# Revit family: PRD_FrankeWS_WCAndWshbsnCmbndUnts_HEAVYDUTYWCWashbasinCombination_HDTX806L_HDTX806M_HDTX806R
name_source: partatom
category: Plumbing Fixtures
revit_build: Autodesk Revit 2018 (Build: 20190510_1515(x64)
units: mm (PartAtom-declared; Revit-internal decimal feet)

## family parameters
Cut with Voids When Loaded = No
Host = Face
OmniClass Number = 23.45.05.14.31
OmniClass Title = Combination Toilets
Part Type = Normal
Room Calculation Point = No
Round Connector Dimension = Use Diameter
Shared = No

## types (3) — shared parameters
AssetType = Fixed
BodyMaterial = PRD_AR_StainlessSteel_SatinFinished
BodyWidth = 390.00 mm
Category = Pr_40_20_93_86, WC and washbasin combined units
DrainSize = 100 mm  [stored 0.328084 ft]
DurationUnit = year
Finish = Satin finish
FloorFixingJogglePlate = No
FrontAccessPanel = No
IfcExportAs = IfcSanitaryTerminalType
IfcExportType = WASHHANDBASIN
InletSize = DN 15
IntakeSize = 15  [stored 0.0492126 ft]
IntegralAccessories = Including fixing material
Manufacturer = KWC Group AG
ManufacturerName = KWC Group AG
ManufacturerURL = www.kwc.com
Material = stainless steel
MaterialCode = 1.4301 Chrome Nickel steel V2A
MaterialThicknessBody = 2.00 mm
MaterialThicknessWC = 1.50 mm
Mounting = BackToWall
NBSDescription = WC and washbasin combined units
NBSReference = 45-35-70/410
NominalHeight = 1000 mm  [stored 3.28084 ft]
OutletSize = DN 100
Overflow = No
PipeworkMaterial = Stainless steel
ProductInformation = https://pim.kwc.com
SelfClosingPushButtons = Electronical
ShroudDesign = Round shape
SoapDish = No
SpoutLength = 83.00 mm
TailorMade = No
TapWithIntegratedBubbler = No
ToiletRollHolderDiameter = 153.00 mm
TypeOfFlushingFitting = WC cistern
TypeOfMounting = Bolt mounting
TypeOfToiletSeat = No seat
TypeOfWC = Floor standing
URL = www.kwc.com
Uniclass2015Code = Pr_40_20_93_86
Uniclass2015Title = WC and washbasin combined units
Uniclass2015Version = Products v1.23
UpperEdgeOfBasinHeight = 850.00 mm
UpstandDepth = 20.00 mm
UpstandHeight = 150.00 mm
Version = 1
WCHeight = 400.00 mm
WarrantyDurationUnit = year
WashHandBasinType = HandRinse
WasteSize = 100  [stored 0.328084 ft]
zero-valued in all types: Default Elevation, MountingOffset

## per-type parameters (varying)
| type | BIMObjectName | Description | Features | GrossWeight | L | M | ModelNumber | Name | NetWeight | NominalDepth | NominalWidth | ProductCode | R | Size | WCPosition |
| HDTX806L | PRD_AR_WCAndWashbasinCombinedUnits_HEAVYDUTYWCWashbasinCombination_HDTX806L | Chromium nickel steel WC wash basin combination, satin finish surface for installing outside a utility room accessible from the back with remotely controlled tap components for fitting in the utility room, fixing from the back with threaded pins. Mounting stand, material thickness 2 mm with elevated rear wall including wall outlet and piezo button with start/stop function, with seamless welded WC paper compartment and seamless moulded wash basin with trap, outlet DN 40. WC pan, material thickness 1.6 mm with full-length skirting, arranged on the left 45 degrees, bowl rim where nothing can hide with piezo button for WC flushing, flushing certified pursuant to EN 997, horizontal outlet at the back DN 100. With solenoid to connect to premixed hot water or cold water. Condensation water-proof concealed cistern with single flush technology (9 or 6 litres) Supply voltage 24 V DC Including fixing material. | Mounting stand, material thickness 2 mm with elevated rear wall including wall outlet and piezo button with start/stop function. WC position on the left | 57.00 kg | Yes | No | 2000100956 | HEAVY-DUTY WC and washbasin combined units HDTX806L | 52.00 kg | 670 mm  [stored 2.19816 ft] | 700 mm  [stored 2.29659 ft] |  | No | 700 x 1000 x 670 mm (W x H x D) | Left |
| HDTX806M | PRD_AR_WCAndWashbasinCombinedUnits_HEAVYDUTYWCWashbasinCombination_HDTX806M | Chromium nickel steel WC wash basin combination, satin finish surface for installing outside a utility room accessible from the back with remotely controlled tap components for fitting in the utility room, fixing from the back with threaded pins. Mounting stand, material thickness 2 mm with elevated rear wall including wall outlet and piezo button with start/stop function, with seamless welded WC paper compartment and seamless moulded wash basin with trap, outlet DN 40. WC pan, material thickness 1.6 mm with full-length skirting, arranged in the middle 90 degrees, bowl rim where nothing can hide with piezo button for WC flushing, flushing certified pursuant to EN 997, horizontal outlet at the back DIN 100. With solenoid to connect to premixed hot water or cold water. Condensation water-proof concealed cistern with single flush technology (9 or 6 litres) Supply voltage 24 V DC Including fixing material. | Mounting stand, material thickness 2 mm with elevated rear wall including wall outlet and piezo button with start/stop function. WC position in the middle | 52.00 kg | No | Yes | 2000100957 | HEAVY-DUTY WC and washbasin combined units HDTX806M | 47.00 kg | 780 mm  [stored 2.55906 ft] | 390 mm  [stored 1.27953 ft] | 206.0472.804 | No | 390 x 1000 x 780 mm (W x H x D) | Middle |
| HDTX806R | PRD_AR_WCAndWashbasinCombinedUnits_HEAVYDUTYWCWashbasinCombination_HDTX806R | Chromium nickel steel WC wash basin combination, satin finish surface for installing outside a utility room accessible from the back with remotely controlled tap components for fitting in the utility room, fixing from the back with threaded pins. Mounting stand, material thickness 2 mm with elevated rear wall including wall outlet and piezo button with start/stop function, with seamless welded WC paper compartment and seamless moulded wash basin with trap, outlet DN 40. WC pan, material thickness 1.6 mm with full-length skirting, arranged on the right 45 degrees, bowl rim where nothing can hide with piezo button for WC flushing, flushing certified pursuant to EN 997, horizontal outlet at the back DN 100. With solenoid to connect to premixed hot water or cold water. Condensation water-proof concealed cistern with single flush technology (9 or 6 litres) Supply voltage 24 V DC Including fixing material. | Mounting stand, material thickness 2 mm with elevated rear wall including wall outlet and piezo button with start/stop function. WC position on the right | 55.00 kg | No | No | 2000100958 | HEAVY-DUTY WC and washbasin combined units HDTX806R | 40.00 kg | 670 mm  [stored 2.19816 ft] | 700 mm  [stored 2.29659 ft] |  | Yes | 700 x 1000 x 670 mm (W x H x D) | Right |

note: column(s) folded — value = type name in every type: Model, ModelReference

note: [stored X ft] marks values corroborated as IEEE doubles in the binary element streams (Revit-internal decimal feet)

## geometry (parser evidence)
native form markers: Sweep x2
no freeform markers — native parametric forms only
